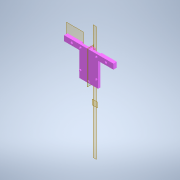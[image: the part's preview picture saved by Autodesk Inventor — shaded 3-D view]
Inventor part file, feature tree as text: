
AUTODESK INVENTOR PART (.ipt)
format: ipt  version: 2020 (Build 240168000, 168)  size: 356,864 bytes
history: native  units: mm
features: other x15, reference x15, sketch x13, extrude x10, projected_geometry x9, hole x3, mirror x1
ambient origin geometry x8: Origin, YZ Plane, XZ Plane, XY Plane, X Axis, Y Axis, Z Axis, Center Point
bodies: Body1 (feature_tree)
feature tree (66):
  other  "솔리드1"
  other  "작업 평면1"
  extrude  "돌출1"  Depth=0.2mm
  other  "작업 평면2"
  extrude  "돌출2"  Depth=10.0mm TaperAngle=0.0deg
  sketch  "스케치3"
  sketch  "스케치4"
  other  "작업 평면3"
  extrude  "돌출4"  Depth=10.0mm TaperAngle=0.0deg
  other  "작업 평면4"
  hole  "구멍1"  [1 undecoded]
  extrude  "돌출5"  Depth=8.0mm
  extrude  "돌출6"  Depth=4.2mm TaperAngle=0.0deg
  extrude  "돌출7"  Depth=84.0mm
  hole  "구멍2"  [1 undecoded]
  other  "작업 평면5"
  mirror  "미러1"
  sketch  "스케치9"
  other  "작업 평면6"
  extrude  "돌출8"  Depth=10.0mm
  extrude  "돌출9"  Depth=5.5mm
  hole  "구멍3"  [1 undecoded]
  extrude  "돌출10"  Depth=8.0mm TaperAngle=0.0deg
  extrude  "돌출11"  Depth=5.0mm TaperAngle=0.0deg
  sketch  "스케치1"
  reference  "참조1"
  reference  "참조2"
  reference  "참조3"
  reference  "참조4"
  reference  "참조5"
  reference  "참조6"
  reference  "참조7"
  reference  "참조8"
  reference  "참조9"
  reference  "참조10"
  sketch  "스케치2"
  reference  "참조11"
  reference  "참조12"
  reference  "참조13"
  reference  "참조14"
  projected_geometry  "투영된 루프1"
  reference  "참조15"
  projected_geometry  "투영된 루프2"
  sketch  "스케치5"
  projected_geometry  "투영된 루프3"
  sketch  "스케치6"
  sketch  "스케치7"
  projected_geometry  "투영된 루프4"
  sketch  "스케치8"
  projected_geometry  "투영된 루프5"
  projected_geometry  "투영된 루프6"
  sketch  "스케치12"
  sketch  "스케치13"
  projected_geometry  "투영된 루프7"
  sketch  "스케치14"
  projected_geometry  "투영된 루프8"
  sketch  "스케치16"
  projected_geometry  "투영된 루프9"
  parser-record x1  (decoder bookkeeping rows leaked as tree rows — omitted from the tree; the rows remain in map.json)
  other  "v6.iam"
  other  "AL_profile_final:1"
  other  "Battery_MIR:1"
  other  "AL_profile_final:2"
  other  "caster_wheel_mount:1"
  other  "center_tray_top:1"
  other  "Battery:1"
note: 3 required parameter values undecoded (feature->parameter linkage not recoverable at this tier; creation-order binding heuristic only, values carry confidence <= 0.55)
note: 1 file-system path scrubbed to <path> (originals preserved in map.json)
